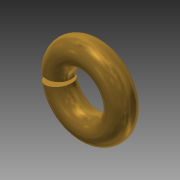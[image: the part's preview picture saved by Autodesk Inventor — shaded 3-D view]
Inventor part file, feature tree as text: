
AUTODESK INVENTOR PART (.ipt)
format: ipt  version: 2015 (Build 190159000, 159)  size: 137,728 bytes
history: native  units: mm
features: revolve x1, sketch x1
ambient origin geometry x8: Origin, YZ Plane, XZ Plane, XY Plane, X Axis, Y Axis, Z Axis, Center Point
bodies: 实体1 (feature_tree)
feature tree (2):
  revolve  "旋转1"  [1 undecoded]
  sketch  "草图1"  dims[d0=4.0mm d1=61.086524mm d2=5.0mm]
note: 1 required parameter value undecoded (feature->parameter linkage not recoverable at this tier; creation-order binding heuristic only, values carry confidence <= 0.55)
